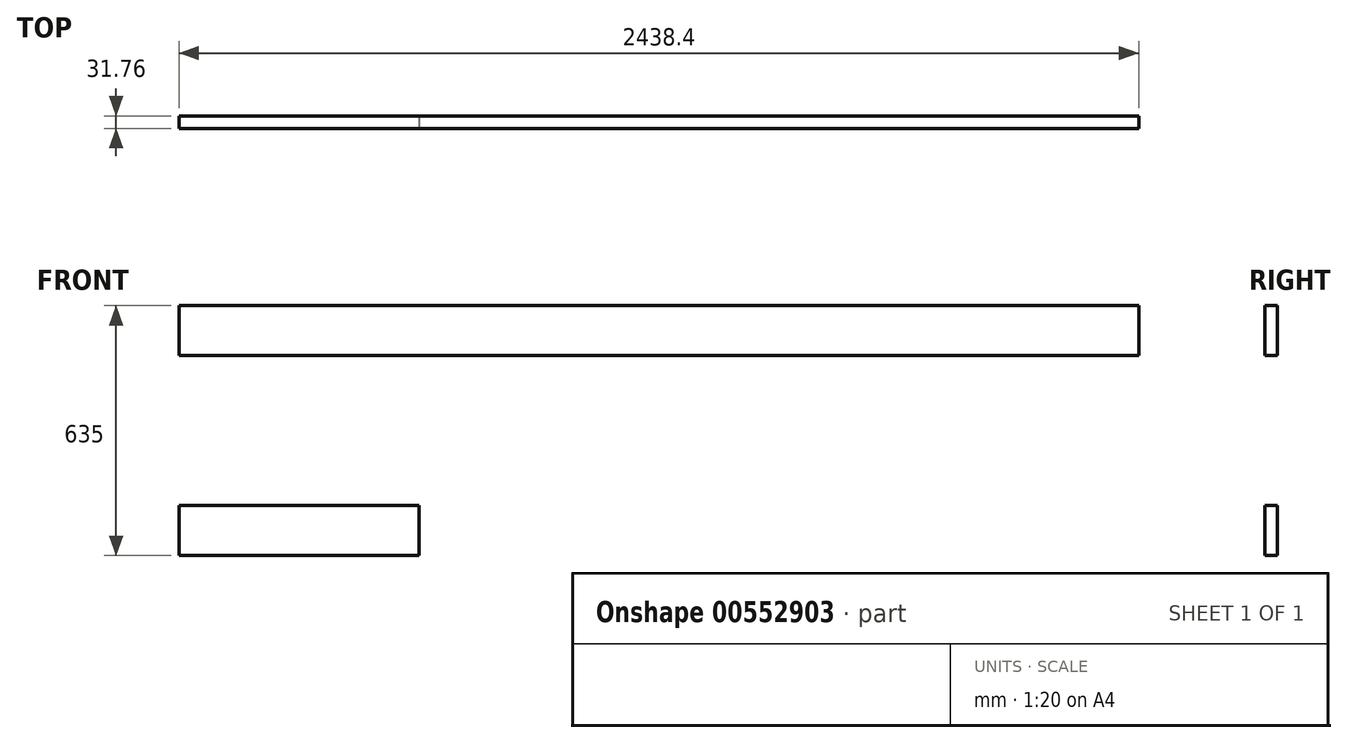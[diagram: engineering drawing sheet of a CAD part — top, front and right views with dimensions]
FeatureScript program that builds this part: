
annotation { "Feature Type Name" : "Feature", "Feature Type Description" : "" }
export const myFeature = defineFeature(function(context is Context, id is Id, definition is map)
    precondition{}
    {
        {
            var Q0;
            Q0=qCreatedBy(makeId("Front.planeOp"),FACE);
            var sketch = newSketch(context, id + "F0", { "sketchPlane" : qUnion([Q0])});
            skLineSegment(sketch, "E0.bottom", {"start": v(1219.2, 63.5) * mm, "end": v(-1219.2, 63.5) * mm});
            skLineSegment(sketch, "E0.top", {"start": v(1219.2, -63.5) * mm, "end": v(-1219.2, -63.5) * mm});
            skLineSegment(sketch, "E0.left", {"start": v(1219.2, 63.5) * mm, "end": v(1219.2, -63.5) * mm});
            skLineSegment(sketch, "E0.right", {"start": v(-1219.2, 63.5) * mm, "end": v(-1219.2, -63.5) * mm});
            skPoint(sketch, "E0.middle", {"position": v(0, 0) * mm});
            skSolve(sketch);
        }
        {
            var Q0;
            Q0 = qSketchRegion(id + "F0", true);
            extrude(context, id + "F1", {"entities" : qUnion([Q0]), "endBound" : BoundingType.SYMMETRIC, "depth" : 31.75 * mm, "offsetDistance" : 25.4 * mm});
        }
        {
            var Q0;
            Q0=makeQuery(id+"F1.opExtrude","SWEPT_BODY",BODY,{"disambiguationData":[OSD([sQuery(id+"F0.wireOp",EDGE,"E0.bottom"),sQuery(id+"F0.wireOp",EDGE,"E0.top"),sQuery(id+"F0.wireOp",EDGE,"E0.left"),sQuery(id+"F0.wireOp",EDGE,"E0.right")])]});
            transform(context, id + "F2", {"entities" : qUnion([Q0]), "transformType" : TransformType.TRANSLATION_3D, "dx" : 0 * mm, "dy" : 0 * mm, "dz" : -508 * mm, "makeCopy" : true});
        }
        {
            var Q0;
            Q0=makeQuery(id+"F2.opPattern","COPY",FACE,{"derivedFrom":makeQuery(id+"F1.opExtrude","CAP_FACE",FACE,{"disambiguationData":[OSD([sQuery(id+"F0.wireOp",EDGE,"E0.bottom"),sQuery(id+"F0.wireOp",EDGE,"E0.top"),sQuery(id+"F0.wireOp",EDGE,"E0.left"),sQuery(id+"F0.wireOp",EDGE,"E0.right")])],"isStart":false}),"instanceName":"1"});
            var sketch = newSketch(context, id + "F3", { "sketchPlane" : qUnion([Q0])});
            skLineSegment(sketch, "E1.bottom", {"start": v(-609.6, -444.5) * mm, "end": v(1219.2, -444.5) * mm});
            skLineSegment(sketch, "E1.top", {"start": v(-609.6, -571.5) * mm, "end": v(1219.2, -571.5) * mm});
            skLineSegment(sketch, "E1.left", {"start": v(-609.6, -444.5) * mm, "end": v(-609.6, -571.5) * mm});
            skLineSegment(sketch, "E1.right", {"start": v(1219.2, -444.5) * mm, "end": v(1219.2, -571.5) * mm});
            skSolve(sketch);
        }
        {
            var Q0;
            Q0 = qSketchRegion(id + "F3", true);
            extrude(context, id + "F4", {"entities" : qUnion([Q0]), "operationType" : NewBodyOperationType.REMOVE, "oppositeDirection" : true, "depth" : 31.75 * mm, "offsetDistance" : 25.4 * mm});
        }
    });
